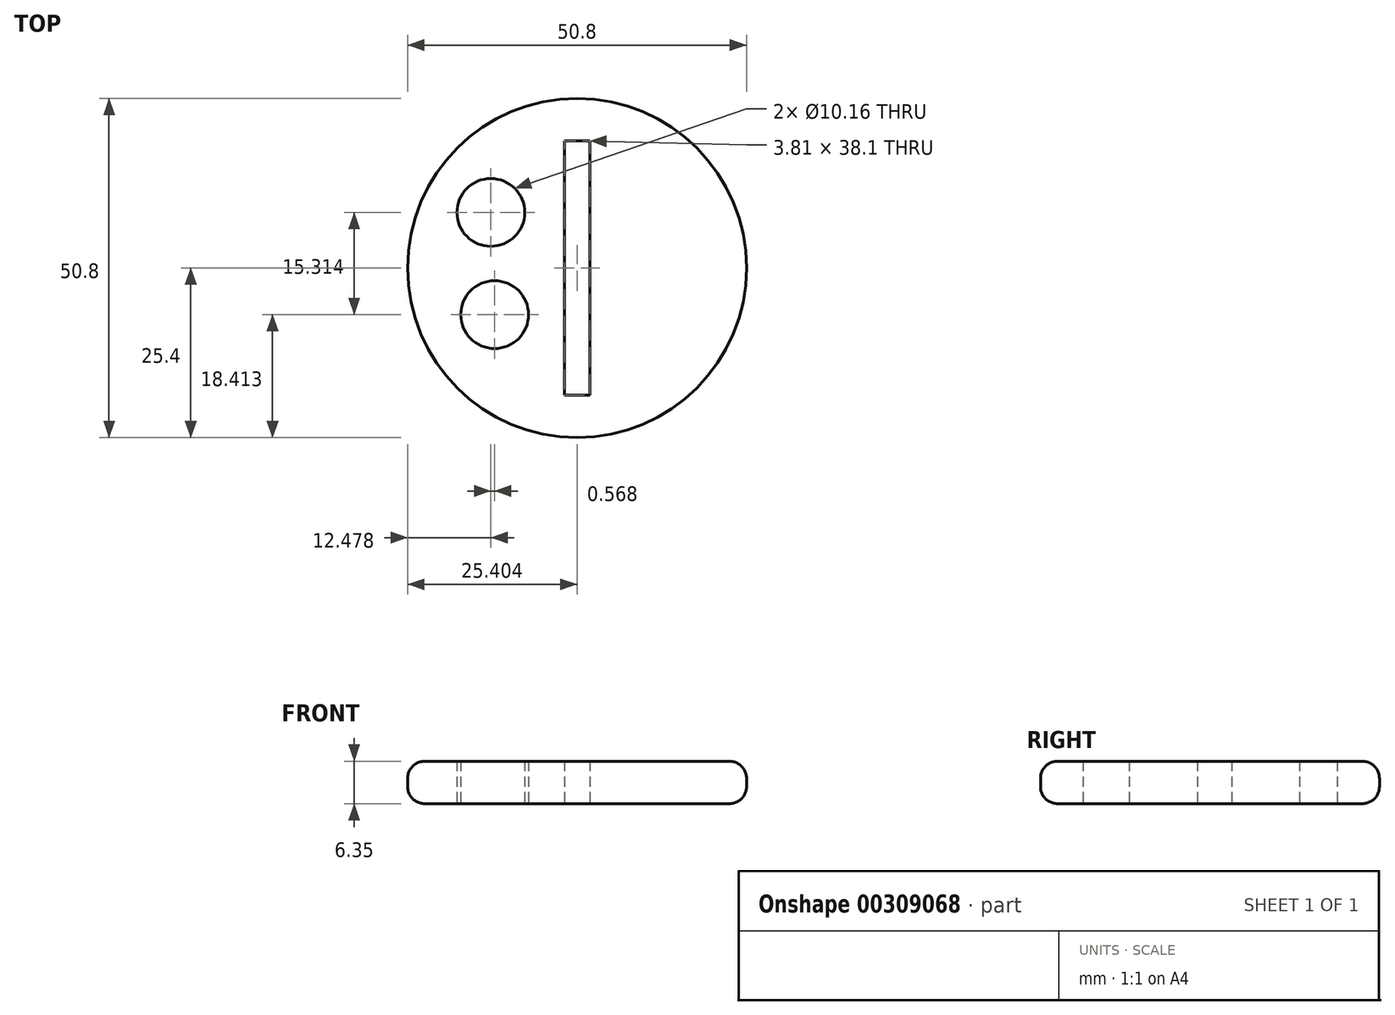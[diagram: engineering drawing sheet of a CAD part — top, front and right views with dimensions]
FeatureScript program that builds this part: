
annotation { "Feature Type Name" : "Feature", "Feature Type Description" : "" }
export const myFeature = defineFeature(function(context is Context, id is Id, definition is map)
    precondition{}
    {
        {
            var Q0;
            Q0=qCreatedBy(makeId("Top.planeOp"),FACE);
            var sketch = newSketch(context, id + "F0", { "sketchPlane" : qUnion([Q0])});
            skCircle(sketch, "E0", {"center": v(-134.29, 19.05) * mm, "radius": 25.4 * mm});
            skLineSegment(sketch, "E1.bottom", {"start": v(-132.38, 0) * mm, "end": v(-136.2, 0) * mm});
            skLineSegment(sketch, "E1.top", {"start": v(-132.38, 38.1) * mm, "end": v(-136.2, 38.1) * mm});
            skLineSegment(sketch, "E1.left", {"start": v(-132.38, 0) * mm, "end": v(-132.38, 38.1) * mm});
            skLineSegment(sketch, "E1.right", {"start": v(-136.2, 0) * mm, "end": v(-136.2, 38.1) * mm});
            skCircle(sketch, "E2", {"center": v(-146.64, 12.06) * mm, "radius": 5.08 * mm});
            skCircle(sketch, "E3", {"center": v(-147.21, 27.38) * mm, "radius": 5.08 * mm});
            skArc(sketch, "E4", {"start": v(-141.56, 12.06) * mm, "mid": v(-142.09, 14.3) * mm, "end": v(-143.55, 16.09) * mm});
            skArc(sketch, "E5", {"start": v(-146.64, 12.06) * mm, "mid": v(-146.6, 12.73) * mm, "end": v(-146.47, 13.38) * mm});
            skSolve(sketch);
        }
        {
            var Q0;
            Q0=makeQuery(id+"F0.imprint","IMPRINT",FACE,{"disambiguationData":[TD([[makeQuery(id+"F0.imprint","IMPRINT",EDGE,{"derivedFrom":sQuery(id+"F0.wireOp",EDGE,"E0")}),1.0]])]});
            extrude(context, id + "F1", {"entities" : qUnion([Q0]), "depth" : 6.35 * mm});
        }
        {
            var Q0;
            Q0=makeQuery(id+"F1.opExtrude","CAP_EDGE",EDGE,{"disambiguationData":[OSD([sQuery(id+"F0.wireOp",EDGE,"E0")])],"isStart":false});
            var Q1;
            Q1=makeQuery(id+"F1.opExtrude","CAP_EDGE",EDGE,{"disambiguationData":[OSD([sQuery(id+"F0.wireOp",EDGE,"E0")])],"isStart":true});
            fillet(context, id + "F2", {"entities" : qUnion([Q0, Q1]), "radius" : 2.54 * mm, "tangentPropagation" : true, "allowEdgeOverflow" : false});
        }
    });
